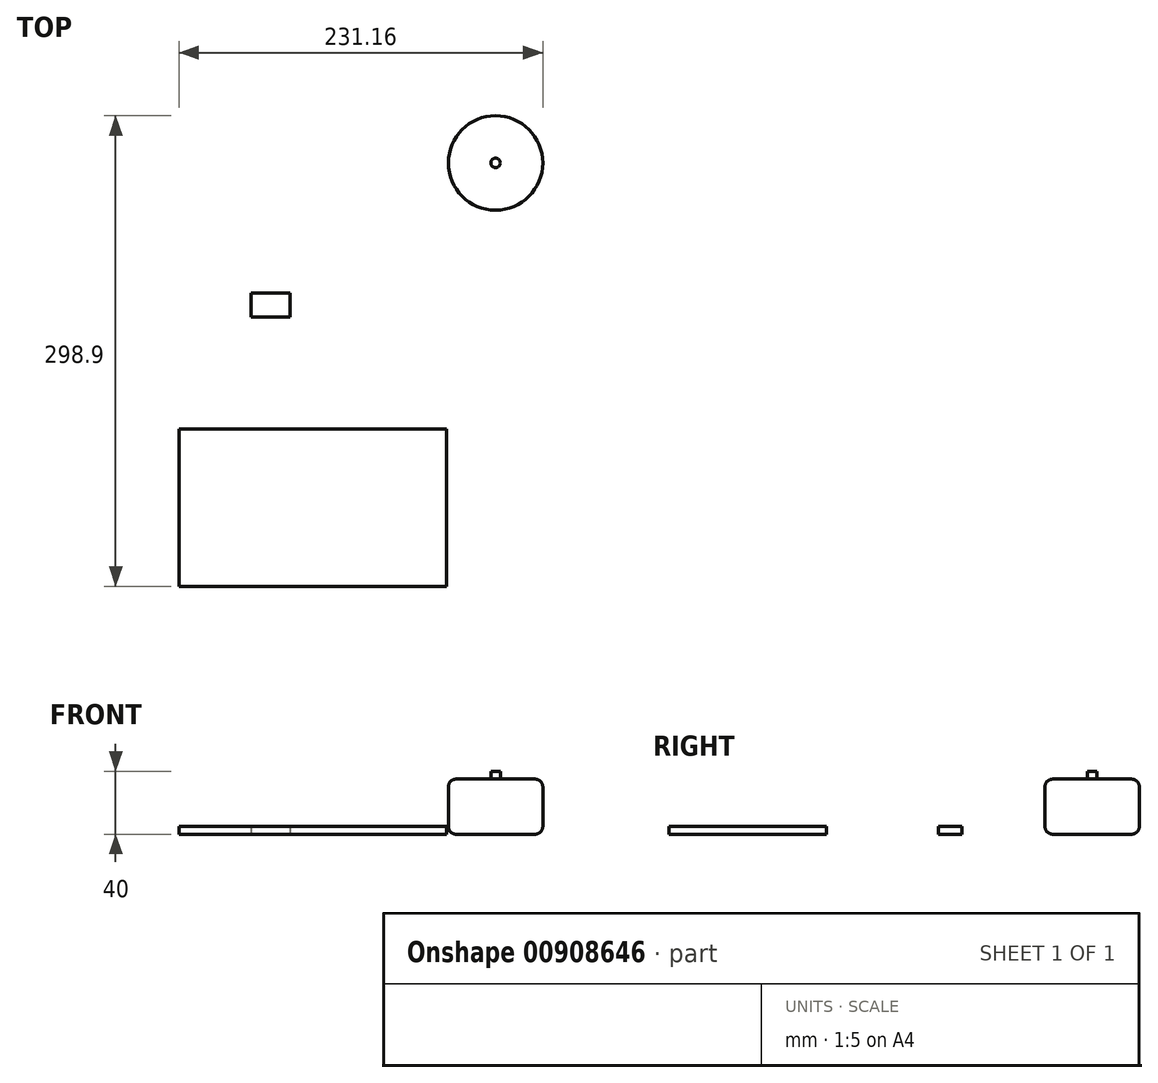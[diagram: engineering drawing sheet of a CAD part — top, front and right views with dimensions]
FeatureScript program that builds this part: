
annotation { "Feature Type Name" : "Feature", "Feature Type Description" : "" }
export const myFeature = defineFeature(function(context is Context, id is Id, definition is map)
    precondition{}
    {
        {
            var Q0;
            Q0=qCreatedBy(makeId("Top.planeOp"),FACE);
            var sketch = newSketch(context, id + "F0", { "sketchPlane" : qUnion([Q0])});
            skLineSegment(sketch, "E0.bottom", {"start": v(-321.83, 75.98) * mm, "end": v(-151.83, 75.98) * mm});
            skLineSegment(sketch, "E0.top", {"start": v(-321.83, -24.02) * mm, "end": v(-151.83, -24.02) * mm});
            skLineSegment(sketch, "E0.left", {"start": v(-321.83, 75.98) * mm, "end": v(-321.83, -24.02) * mm});
            skLineSegment(sketch, "E0.right", {"start": v(-151.83, 75.98) * mm, "end": v(-151.83, -24.02) * mm});
            skSolve(sketch);
        }
        {
            var Q0;
            Q0=makeQuery(id+"F0.imprint","IMPRINT",FACE,{"disambiguationData":[TD([[makeQuery(id+"F0.imprint","IMPRINT",EDGE,{"derivedFrom":sQuery(id+"F0.wireOp",EDGE,"E0.bottom")}),-1.0]])]});
            extrude(context, id + "F1", {"entities" : qUnion([Q0]), "depth" : 5 * mm, "offsetDistance" : 25 * mm});
        }
        {
            var Q0;
            Q0=qCreatedBy(makeId("Top.planeOp"),FACE);
            var sketch = newSketch(context, id + "F2", { "sketchPlane" : qUnion([Q0])});
            skCircle(sketch, "E1", {"center": v(-120.67, 244.88) * mm, "radius": 30 * mm});
            skSolve(sketch);
        }
        {
            var Q0;
            Q0=makeQuery(id+"F2.imprint","IMPRINT",FACE,{"disambiguationData":[TD([[makeQuery(id+"F2.imprint","IMPRINT",EDGE,{"derivedFrom":sQuery(id+"F2.wireOp",EDGE,"E1")}),1.0]])]});
            extrude(context, id + "F3", {"entities" : qUnion([Q0]), "depth" : 35 * mm, "offsetDistance" : 25 * mm});
        }
        {
            var Q0;
            Q0=makeQuery(id+"F3.opExtrude","CAP_FACE",FACE,{"disambiguationData":[OSD([sQuery(id+"F2.wireOp",EDGE,"E1")])],"isStart":false});
            var Q1;
            Q1=makeQuery(id+"F3.opExtrude","SWEPT_FACE",FACE,{"disambiguationData":[OSD([sQuery(id+"F2.wireOp",EDGE,"E1")])]});
            fillet(context, id + "F4", {"entities" : qUnion([Q0, Q1]), "radius" : 5 * mm, "tangentPropagation" : true, "allowEdgeOverflow" : false});
        }
        {
            var Q0;
            Q0=makeQuery(id+"F3.opExtrude","CAP_FACE",FACE,{"disambiguationData":[OSD([sQuery(id+"F2.wireOp",EDGE,"E1")])],"isStart":false});
            var sketch = newSketch(context, id + "F5", { "sketchPlane" : qUnion([Q0])});
            skCircle(sketch, "E2", {"center": v(-120.67, 244.88) * mm, "radius": 3 * mm});
            skSolve(sketch);
        }
        {
            var Q0;
            Q0=makeQuery(id+"F5.imprint","IMPRINT",FACE,{"disambiguationData":[TD([[makeQuery(id+"F5.imprint","IMPRINT",EDGE,{"derivedFrom":sQuery(id+"F5.wireOp",EDGE,"E2")}),1.0]])]});
            extrude(context, id + "F6", {"entities" : qUnion([Q0]), "operationType" : NewBodyOperationType.ADD, "depth" : 5 * mm, "offsetDistance" : 25 * mm});
        }
        {
            var Q0;
            Q0=qCreatedBy(makeId("Top.planeOp"),FACE);
            var sketch = newSketch(context, id + "F7", { "sketchPlane" : qUnion([Q0])});
            skLineSegment(sketch, "E3.bottom", {"start": v(-276.1, 162.13) * mm, "end": v(-251.1, 162.13) * mm});
            skLineSegment(sketch, "E3.top", {"start": v(-276.1, 147.13) * mm, "end": v(-251.1, 147.13) * mm});
            skLineSegment(sketch, "E3.left", {"start": v(-276.1, 162.13) * mm, "end": v(-276.1, 147.13) * mm});
            skLineSegment(sketch, "E3.right", {"start": v(-251.1, 162.13) * mm, "end": v(-251.1, 147.13) * mm});
            skSolve(sketch);
        }
        {
            var Q0;
            Q0=makeQuery(id+"F7.imprint","IMPRINT",FACE,{"disambiguationData":[TD([[makeQuery(id+"F7.imprint","IMPRINT",EDGE,{"derivedFrom":sQuery(id+"F7.wireOp",EDGE,"E3.bottom")}),-1.0]])]});
            extrude(context, id + "F8", {"entities" : qUnion([Q0]), "depth" : 5 * mm, "offsetDistance" : 25 * mm});
        }
    });
